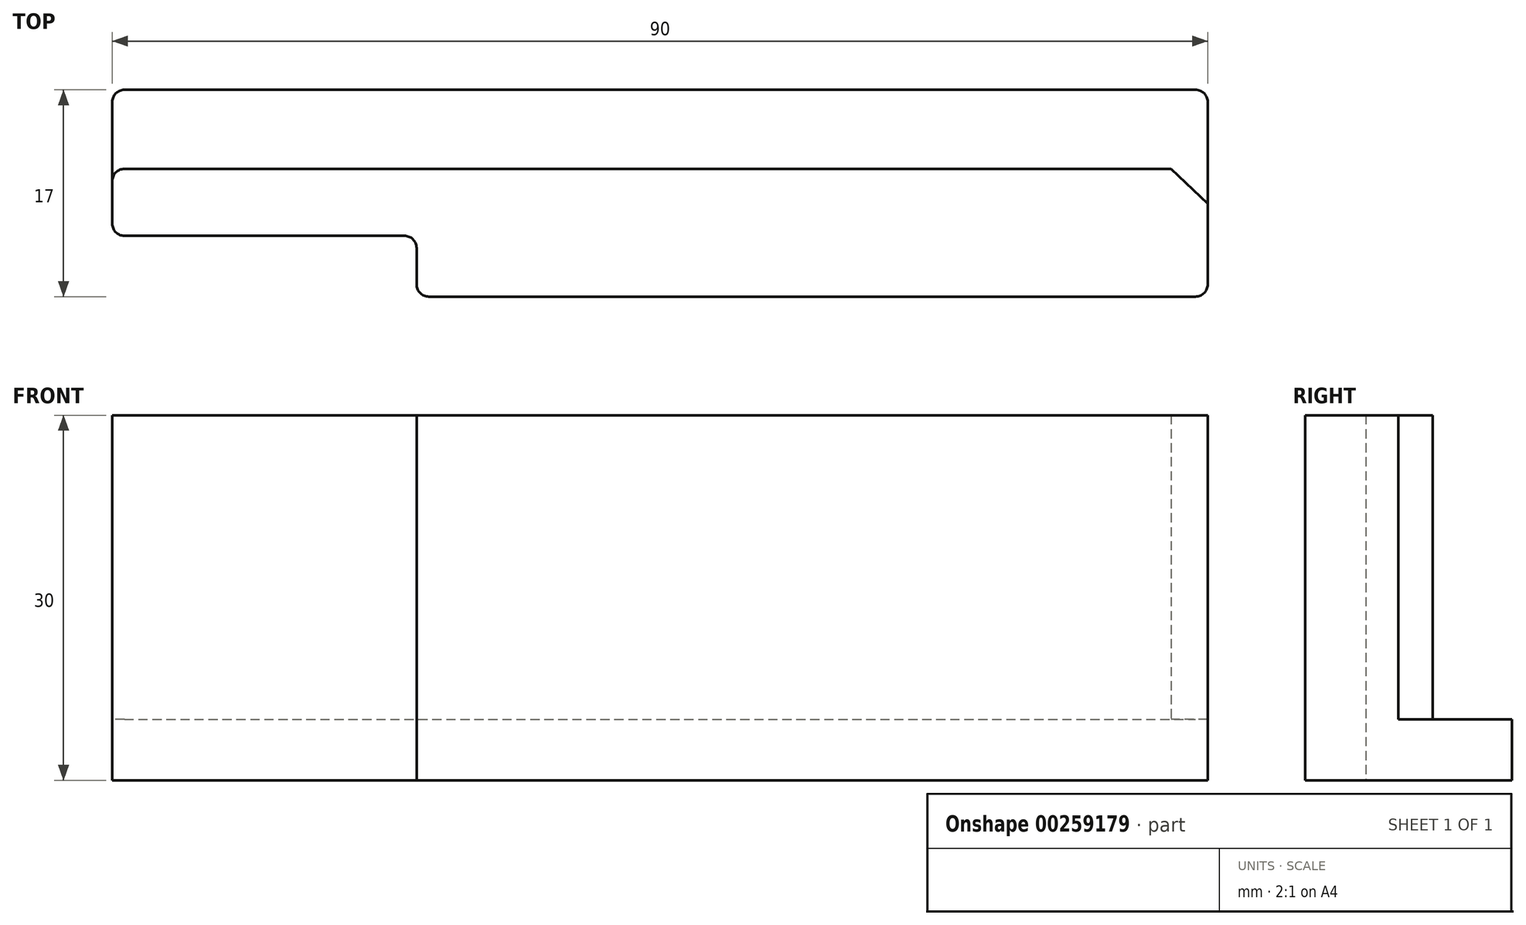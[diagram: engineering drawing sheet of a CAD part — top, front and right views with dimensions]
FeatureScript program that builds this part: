
annotation { "Feature Type Name" : "Feature", "Feature Type Description" : "" }
export const myFeature = defineFeature(function(context is Context, id is Id, definition is map)
    precondition{}
    {
        {
            var Q0;
            Q0=qCreatedBy(makeId("Top.planeOp"),FACE);
            var sketch = newSketch(context, id + "F0", { "sketchPlane" : qUnion([Q0])});
            skLineSegment(sketch, "E0.bottom", {"start": v(-31.5, -5.25) * mm, "end": v(31.5, -5.25) * mm});
            skLineSegment(sketch, "E0.top", {"start": v(-31.5, 5.25) * mm, "end": v(29.5, 5.25) * mm});
            skLineSegment(sketch, "E0.left", {"start": v(-32.5, -4.25) * mm, "end": v(-32.5, -1.25) * mm});
            skLineSegment(sketch, "E0.right", {"start": v(32.5, -4.25) * mm, "end": v(32.5, 2.4) * mm});
            skPoint(sketch, "E1.visualSharp", {"position": v(-32.5, 5.25) * mm});
            skPoint(sketch, "E2.visualSharp", {"position": v(-32.5, -5.25) * mm});
            skArc(sketch, "E2.filletArc", {"start": v(-32.5, -4.25) * mm, "mid": v(-32.2, -4.96) * mm, "end": v(-31.5, -5.25) * mm});
            skPoint(sketch, "E3.visualSharp", {"position": v(32.5, -5.25) * mm});
            skArc(sketch, "E3.filletArc", {"start": v(31.5, -5.25) * mm, "mid": v(32.2, -4.96) * mm, "end": v(32.5, -4.25) * mm});
            skLineSegment(sketch, "E4", {"start": v(32.5, 2.4) * mm, "end": v(29.5, 5.25) * mm});
            skPoint(sketch, "E5.orphan", {"position": v(32.5, 5.25) * mm});
            skLineSegment(sketch, "E6", {"start": v(-32.5, 5.25) * mm, "end": v(-56.5, 5.25) * mm});
            skLineSegment(sketch, "E7", {"start": v(-57.5, 4.25) * mm, "end": v(-57.5, 0.75) * mm});
            skLineSegment(sketch, "E8", {"start": v(-56.5, -0.25) * mm, "end": v(-33.5, -0.25) * mm});
            skLineSegment(sketch, "E9", {"start": v(-31.5, 5.25) * mm, "end": v(-32.5, 5.25) * mm});
            skPoint(sketch, "E10.visualSharp", {"position": v(-32.5, -0.25) * mm});
            skArc(sketch, "E10.filletArc", {"start": v(-32.5, -1.25) * mm, "mid": v(-32.8, -0.54) * mm, "end": v(-33.5, -0.25) * mm});
            skPoint(sketch, "E11.visualSharp", {"position": v(-57.5, -0.25) * mm});
            skArc(sketch, "E11.filletArc", {"start": v(-57.5, 0.75) * mm, "mid": v(-57.2, 0.04) * mm, "end": v(-56.5, -0.25) * mm});
            skPoint(sketch, "E12.visualSharp", {"position": v(-57.5, 5.25) * mm});
            skArc(sketch, "E12.filletArc", {"start": v(-56.5, 5.25) * mm, "mid": v(-57.2, 4.96) * mm, "end": v(-57.5, 4.25) * mm});
            skSolve(sketch);
        }
        {
            var Q0;
            Q0=makeQuery(id+"F0.imprint","IMPRINT",FACE,{"disambiguationData":[TD([[makeQuery(id+"F0.imprint","IMPRINT",EDGE,{"derivedFrom":sQuery(id+"F0.wireOp",EDGE,"E0.bottom")}),1.0]])]});
            extrude(context, id + "F1", {"entities" : qUnion([Q0]), "depth" : 25 * mm});
        }
        {
            var Q0;
            Q0=qCreatedBy(makeId("Top.planeOp"),FACE);
            var sketch = newSketch(context, id + "F2", { "sketchPlane" : qUnion([Q0])});
            skLineSegment(sketch, "E13.bottom", {"start": v(-31.5, -5.25) * mm, "end": v(31.5, -5.25) * mm});
            skLineSegment(sketch, "E13.top", {"start": v(-31.5, 11.75) * mm, "end": v(31.5, 11.75) * mm});
            skLineSegment(sketch, "E13.left", {"start": v(-32.5, -4.25) * mm, "end": v(-32.5, -1.25) * mm});
            skLineSegment(sketch, "E13.right", {"start": v(32.5, -4.25) * mm, "end": v(32.5, 10.75) * mm});
            skPoint(sketch, "E14.visualSharp", {"position": v(-32.5, -5.25) * mm});
            skArc(sketch, "E14.filletArc", {"start": v(-32.5, -4.25) * mm, "mid": v(-32.2, -4.96) * mm, "end": v(-31.5, -5.25) * mm});
            skPoint(sketch, "E15.visualSharp", {"position": v(-32.5, 11.75) * mm});
            skPoint(sketch, "E16.visualSharp", {"position": v(32.5, 11.75) * mm});
            skArc(sketch, "E16.filletArc", {"start": v(32.5, 10.75) * mm, "mid": v(32.2, 11.46) * mm, "end": v(31.5, 11.75) * mm});
            skPoint(sketch, "E17.visualSharp", {"position": v(32.5, -5.25) * mm});
            skArc(sketch, "E17.filletArc", {"start": v(31.5, -5.25) * mm, "mid": v(32.2, -4.96) * mm, "end": v(32.5, -4.25) * mm});
            skLineSegment(sketch, "E18", {"start": v(-31.5, 11.75) * mm, "end": v(-32.5, 11.75) * mm});
            skLineSegment(sketch, "E19", {"start": v(-57.5, 10.75) * mm, "end": v(-57.5, 0.75) * mm});
            skLineSegment(sketch, "E20", {"start": v(-56.5, -0.25) * mm, "end": v(-33.5, -0.25) * mm});
            skLineSegment(sketch, "E21", {"start": v(-56.5, 11.75) * mm, "end": v(-32.5, 11.75) * mm});
            skPoint(sketch, "E22.visualSharp", {"position": v(-32.5, -0.25) * mm});
            skArc(sketch, "E22.filletArc", {"start": v(-32.5, -1.25) * mm, "mid": v(-32.8, -0.54) * mm, "end": v(-33.5, -0.25) * mm});
            skPoint(sketch, "E23.visualSharp", {"position": v(-57.5, -0.25) * mm});
            skArc(sketch, "E23.filletArc", {"start": v(-57.5, 0.75) * mm, "mid": v(-57.2, 0.04) * mm, "end": v(-56.5, -0.25) * mm});
            skPoint(sketch, "E24.visualSharp", {"position": v(-57.5, 11.75) * mm});
            skArc(sketch, "E24.filletArc", {"start": v(-56.5, 11.75) * mm, "mid": v(-57.2, 11.46) * mm, "end": v(-57.5, 10.75) * mm});
            skSolve(sketch);
        }
        {
            var Q0;
            Q0=makeQuery(id+"F2.imprint","IMPRINT",FACE,{"disambiguationData":[TD([[makeQuery(id+"F2.imprint","IMPRINT",EDGE,{"derivedFrom":sQuery(id+"F2.wireOp",EDGE,"E13.bottom")}),1.0]])]});
            extrude(context, id + "F3", {"entities" : qUnion([Q0]), "operationType" : NewBodyOperationType.ADD, "oppositeDirection" : true, "depth" : 5 * mm});
        }
    });
